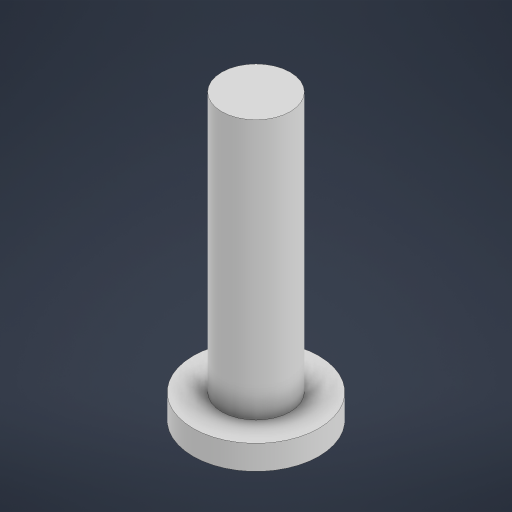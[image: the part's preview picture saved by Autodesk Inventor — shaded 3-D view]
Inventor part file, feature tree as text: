
AUTODESK INVENTOR PART (.ipt)
format: ipt  version: 2023 (Build 270158030, 158C)  size: 176,128 bytes
history: native  units: in
note: dims shown in document units (in); Inventor stores cm internally (conversion verified against a paired STEP export)
features: extrude x2, sketch x2
ambient origin geometry x8: Origin, YZ Plane, XZ Plane, XY Plane, X Axis, Y Axis, Z Axis, Center Point
bodies: Body1 (feature_tree)
feature tree (4):
  extrude  "Extrusion4"  Depth=0.1102in TaperAngle=0.0deg
  extrude  "Extrusion5"  Depth=1.1811in TaperAngle=0.0deg
  sketch  "Sketch5"  dims[d9=0.5709in d10=0.1102in d11=0.0in]
  sketch  "Sketch6"  dims[d12=0.311in d13=1.1811in d14=0.0in]
